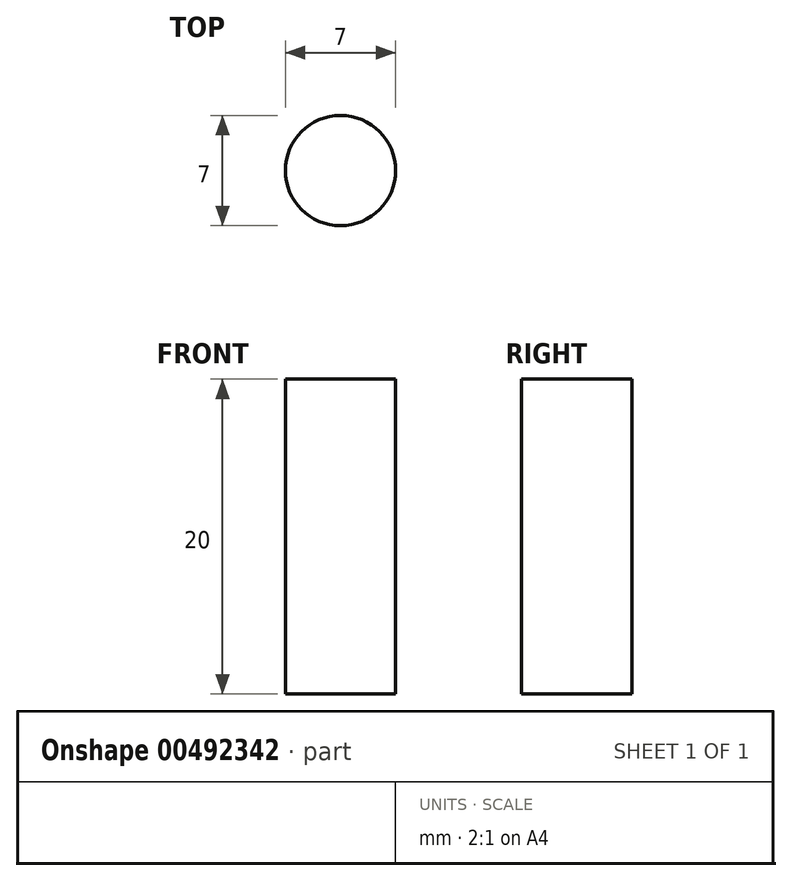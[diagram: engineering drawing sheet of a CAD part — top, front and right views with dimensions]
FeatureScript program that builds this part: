
annotation { "Feature Type Name" : "Feature", "Feature Type Description" : "" }
export const myFeature = defineFeature(function(context is Context, id is Id, definition is map)
    precondition{}
    {
        {
            var Q0;
            Q0=qCreatedBy(makeId("Top.planeOp"),FACE);
            var sketch = newSketch(context, id + "F0", { "sketchPlane" : qUnion([Q0])});
            skCircle(sketch, "E0", {"center": v(0, 0) * mm, "radius": 3.5 * mm});
            skSolve(sketch);
        }
        {
            var Q0;
            Q0=makeQuery(id+"F0.imprint","IMPRINT",FACE,{"disambiguationData":[TD([[makeQuery(id+"F0.imprint","IMPRINT",EDGE,{"derivedFrom":sQuery(id+"F0.wireOp",EDGE,"E0")}),1.0]])]});
            var Q1;
            Q1=sQuery(id+"F0.wireOp",EDGE,"E0");
            extrude(context, id + "F1", {"entities" : qUnion([Q0]), "surfaceEntities" : qUnion([Q1]), "depth" : 20 * mm});
        }
    });
